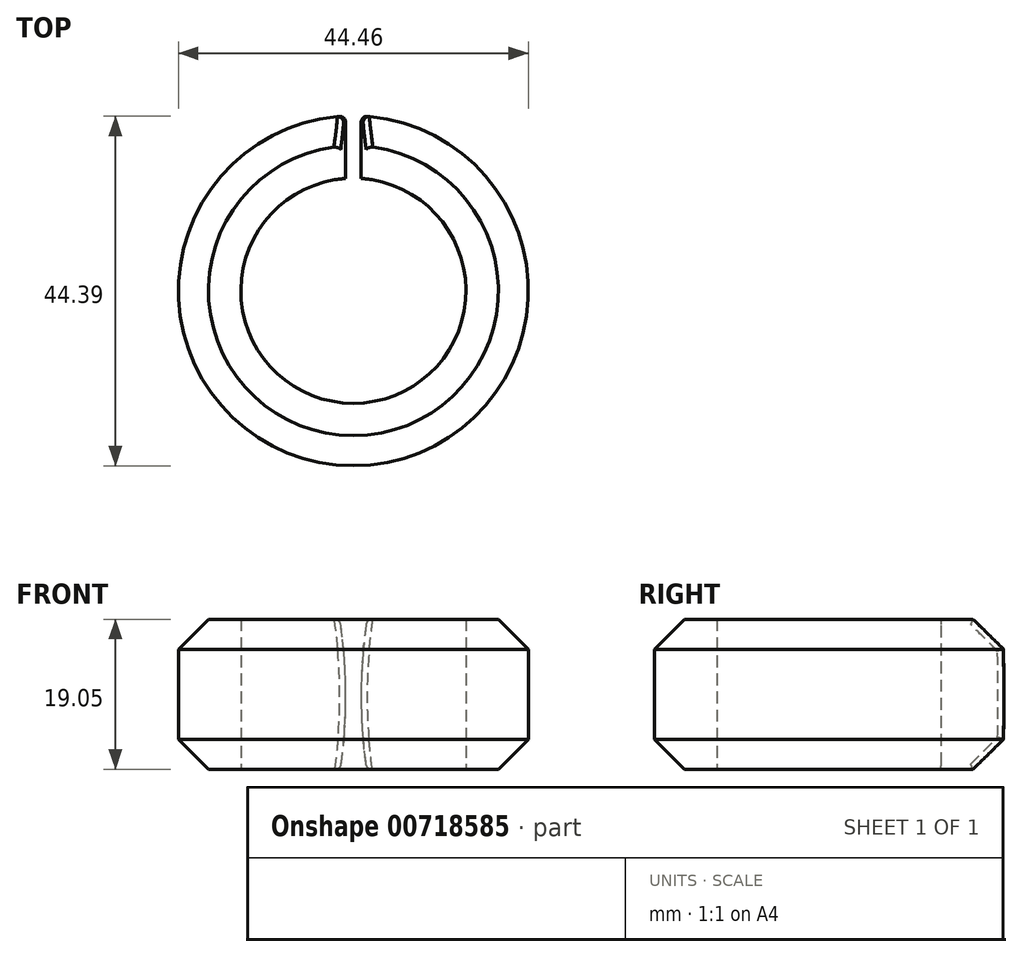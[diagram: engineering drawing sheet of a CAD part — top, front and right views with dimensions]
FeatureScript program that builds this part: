
annotation { "Feature Type Name" : "Feature", "Feature Type Description" : "" }
export const myFeature = defineFeature(function(context is Context, id is Id, definition is map)
    precondition{}
    {
        {
            var Q0;
            Q0=qCreatedBy(makeId("Top.planeOp"),FACE);
            var sketch = newSketch(context, id + "F0", { "sketchPlane" : qUnion([Q0])});
            skCircle(sketch, "E0", {"center": v(0, 0) * mm, "radius": 14.3 * mm});
            skCircle(sketch, "E1", {"center": v(0, 0) * mm, "radius": 22.23 * mm});
            skLineSegment(sketch, "E2.bottom", {"start": v(-0.87, 25.98) * mm, "end": v(0.87, 25.98) * mm});
            skLineSegment(sketch, "E2.top", {"start": v(-0.87, 8.77) * mm, "end": v(0.87, 8.77) * mm});
            skLineSegment(sketch, "E2.left", {"start": v(-0.87, 25.98) * mm, "end": v(-0.87, 8.77) * mm});
            skLineSegment(sketch, "E2.right", {"start": v(0.87, 25.98) * mm, "end": v(0.87, 8.77) * mm});
            skPoint(sketch, "E2.middle", {"position": v(0, 17.37) * mm});
            skSolve(sketch);
        }
        {
            var Q0;
            {var subQ0=sQuery(id+"F0.wireOp",EDGE,"E2.left");var subQ1=sQuery(id+"F0.wireOp",EDGE,"E0");var subQ2=makeQuery(id+"F0.imprint","INTERSECT",VERTEX,{"derivedFrom":[subQ1,subQ0]});Q0=makeQuery(id+"F0.imprint","IMPRINT",FACE,{"disambiguationData":[TD([[makeQuery(id+"F0.imprint","IMPRINT",EDGE,{"disambiguationData":[TD([[subQ2,-1.0]])],"derivedFrom":subQ1}),-1.0]])]});}
            extrude(context, id + "F1", {"entities" : qUnion([Q0]), "depth" : 19.05 * mm, "offsetDistance" : 25.4 * mm});
        }
        {
            var Q0;
            Q0=makeQuery(id+"F1.opExtrude","CAP_EDGE",EDGE,{"disambiguationData":[OSD([sQuery(id+"F0.wireOp",EDGE,"E1")])],"isStart":false});
            var Q1;
            Q1=makeQuery(id+"F1.opExtrude","CAP_EDGE",EDGE,{"disambiguationData":[OSD([sQuery(id+"F0.wireOp",EDGE,"E1")])],"isStart":true});
            chamfer(context, id + "F2", {"entities" : qUnion([Q0, Q1]), "width" : 3.8 * mm, "tangentPropagation" : true});
        }
        {
            var Q0;
            Q0=qCreatedBy(makeId("Front.planeOp"),FACE);
            var sketch = newSketch(context, id + "F3", { "sketchPlane" : qUnion([Q0])});
            skCircle(sketch, "E3", {"center": v(66.15, 9.25) * mm, "radius": 65.17 * mm});
            skCircle(sketch, "E4.MirrorC", {"center": v(-66.15, 9.25) * mm, "radius": 65.17 * mm});
            skLineSegment(sketch, "E5", {"start": v(2.92, 25.04) * mm, "end": v(-2.92, 25.04) * mm});
            skLineSegment(sketch, "E6.MirrorCS", {"start": v(2.92, -5.5) * mm, "end": v(-2.92, -5.5) * mm});
            skSolve(sketch);
        }
        {
            var Q0;
            {var subQ0=sQuery(id+"F3.wireOp",EDGE,"E5");Q0=makeQuery(id+"F3.imprint","IMPRINT",FACE,{"disambiguationData":[TD([[makeQuery(id+"F3.imprint","IMPRINT",EDGE,{"derivedFrom":subQ0}),1.0]])]});}
            extrude(context, id + "F4", {"entities" : qUnion([Q0]), "operationType" : NewBodyOperationType.REMOVE, "oppositeDirection" : true, "depth" : 25.4 * mm, "offsetDistance" : 25.4 * mm});
        }
        {
            var Q0;
            {var subQ0=sQuery(id+"F0.wireOp",EDGE,"E1");Q0=makeQuery(id+"F4.boolean.opBoolean","INTERSECT",EDGE,{"derivedFrom":[makeQuery(id+"F2.opChamfer","BLEND_FACE",FACE,{"disambiguationData":[OSD([subQ0]),TDD([makeQuery(id+"F1.opExtrude","CAP_EDGE",EDGE,{"disambiguationData":[OSD([subQ0])],"isStart":false})])]}),makeQuery(id+"F4.opExtrude","SWEPT_FACE",FACE,{"disambiguationData":[OSD([sQuery(id+"F3.wireOp",EDGE,"E4.MirrorC")])]})]});}
            var Q1;
            {var subQ0=sQuery(id+"F0.wireOp",EDGE,"E1");Q1=makeQuery(id+"F4.boolean.opBoolean","INTERSECT",EDGE,{"derivedFrom":[makeQuery(id+"F2.opChamfer","BLEND_FACE",FACE,{"disambiguationData":[OSD([subQ0]),TDD([makeQuery(id+"F1.opExtrude","CAP_EDGE",EDGE,{"disambiguationData":[OSD([subQ0])],"isStart":false})])]}),makeQuery(id+"F4.opExtrude","SWEPT_FACE",FACE,{"disambiguationData":[OSD([sQuery(id+"F3.wireOp",EDGE,"E3")])]})]});}
            var Q2;
            Q2=makeQuery(id+"F4.boolean.opBoolean","INTERSECT",EDGE,{"derivedFrom":[makeQuery(id+"F1.opExtrude","SWEPT_FACE",FACE,{"disambiguationData":[OSD([sQuery(id+"F0.wireOp",EDGE,"E1")])]}),makeQuery(id+"F4.opExtrude","SWEPT_FACE",FACE,{"disambiguationData":[OSD([sQuery(id+"F3.wireOp",EDGE,"E4.MirrorC")])]})]});
            var Q3;
            Q3=makeQuery(id+"F4.boolean.opBoolean","INTERSECT",EDGE,{"derivedFrom":[makeQuery(id+"F1.opExtrude","SWEPT_FACE",FACE,{"disambiguationData":[OSD([sQuery(id+"F0.wireOp",EDGE,"E1")])]}),makeQuery(id+"F4.opExtrude","SWEPT_FACE",FACE,{"disambiguationData":[OSD([sQuery(id+"F3.wireOp",EDGE,"E3")])]})]});
            var Q4;
            Q4=makeQuery(id+"F4.boolean.opBoolean","INTERSECT",EDGE,{"derivedFrom":[makeQuery(id+"F1.opExtrude","CAP_FACE",FACE,{"disambiguationData":[OSD([sQuery(id+"F0.wireOp",EDGE,"E0"),sQuery(id+"F0.wireOp",EDGE,"E1"),sQuery(id+"F0.wireOp",EDGE,"E2.left"),sQuery(id+"F0.wireOp",EDGE,"E2.right")])],"isStart":false}),makeQuery(id+"F4.opExtrude","SWEPT_FACE",FACE,{"disambiguationData":[OSD([sQuery(id+"F3.wireOp",EDGE,"E3")])]})]});
            var Q5;
            Q5=makeQuery(id+"F4.boolean.opBoolean","INTERSECT",EDGE,{"derivedFrom":[makeQuery(id+"F1.opExtrude","CAP_FACE",FACE,{"disambiguationData":[OSD([sQuery(id+"F0.wireOp",EDGE,"E0"),sQuery(id+"F0.wireOp",EDGE,"E1"),sQuery(id+"F0.wireOp",EDGE,"E2.left"),sQuery(id+"F0.wireOp",EDGE,"E2.right")])],"isStart":false}),makeQuery(id+"F4.opExtrude","SWEPT_FACE",FACE,{"disambiguationData":[OSD([sQuery(id+"F3.wireOp",EDGE,"E4.MirrorC")])]})]});
            var Q6;
            {var subQ0=sQuery(id+"F0.wireOp",EDGE,"E1");Q6=makeQuery(id+"F4.boolean.opBoolean","INTERSECT",EDGE,{"derivedFrom":[makeQuery(id+"F2.opChamfer","BLEND_FACE",FACE,{"disambiguationData":[OSD([subQ0]),TDD([makeQuery(id+"F1.opExtrude","CAP_EDGE",EDGE,{"disambiguationData":[OSD([subQ0])],"isStart":true})])]}),makeQuery(id+"F4.opExtrude","SWEPT_FACE",FACE,{"disambiguationData":[OSD([sQuery(id+"F3.wireOp",EDGE,"E4.MirrorC")])]})]});}
            var Q7;
            Q7=makeQuery(id+"F4.boolean.opBoolean","INTERSECT",EDGE,{"derivedFrom":[makeQuery(id+"F1.opExtrude","CAP_FACE",FACE,{"disambiguationData":[OSD([sQuery(id+"F0.wireOp",EDGE,"E0"),sQuery(id+"F0.wireOp",EDGE,"E1"),sQuery(id+"F0.wireOp",EDGE,"E2.left"),sQuery(id+"F0.wireOp",EDGE,"E2.right")])],"isStart":true}),makeQuery(id+"F4.opExtrude","SWEPT_FACE",FACE,{"disambiguationData":[OSD([sQuery(id+"F3.wireOp",EDGE,"E4.MirrorC")])]})]});
            var Q8;
            {var subQ0=sQuery(id+"F0.wireOp",EDGE,"E1");Q8=makeQuery(id+"F4.boolean.opBoolean","INTERSECT",EDGE,{"derivedFrom":[makeQuery(id+"F2.opChamfer","BLEND_FACE",FACE,{"disambiguationData":[OSD([subQ0]),TDD([makeQuery(id+"F1.opExtrude","CAP_EDGE",EDGE,{"disambiguationData":[OSD([subQ0])],"isStart":true})])]}),makeQuery(id+"F4.opExtrude","SWEPT_FACE",FACE,{"disambiguationData":[OSD([sQuery(id+"F3.wireOp",EDGE,"E3")])]})]});}
            var Q9;
            Q9=makeQuery(id+"F4.boolean.opBoolean","INTERSECT",EDGE,{"derivedFrom":[makeQuery(id+"F1.opExtrude","CAP_FACE",FACE,{"disambiguationData":[OSD([sQuery(id+"F0.wireOp",EDGE,"E0"),sQuery(id+"F0.wireOp",EDGE,"E1"),sQuery(id+"F0.wireOp",EDGE,"E2.left"),sQuery(id+"F0.wireOp",EDGE,"E2.right")])],"isStart":true}),makeQuery(id+"F4.opExtrude","SWEPT_FACE",FACE,{"disambiguationData":[OSD([sQuery(id+"F3.wireOp",EDGE,"E3")])]})]});
            fillet(context, id + "F5", {"entities" : qUnion([Q0, Q1, Q2, Q3, Q4, Q5, Q6, Q7, Q8, Q9]), "radius" : 0.76 * mm, "tangentPropagation" : true, "allowEdgeOverflow" : false});
        }
    });
